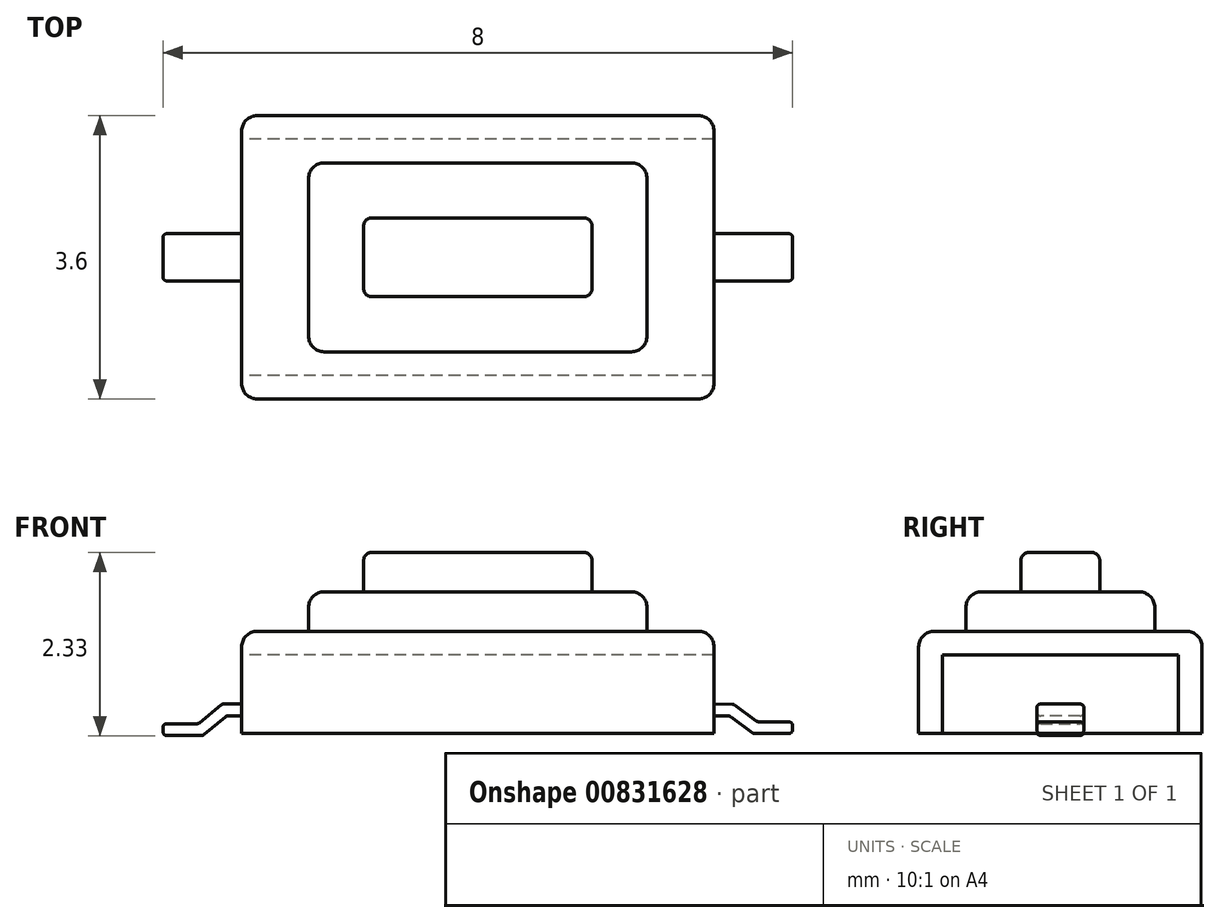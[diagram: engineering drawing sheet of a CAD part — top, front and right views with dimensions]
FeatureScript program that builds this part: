
annotation { "Feature Type Name" : "Feature", "Feature Type Description" : "" }
export const myFeature = defineFeature(function(context is Context, id is Id, definition is map)
    precondition{}
    {
        {
            var Q0;
            Q0=qCreatedBy(makeId("Top.planeOp"),FACE);
            var sketch = newSketch(context, id + "F0", { "sketchPlane" : qUnion([Q0])});
            skLineSegment(sketch, "E0.bottom", {"start": v(3, -1.5) * mm, "end": v(-3, -1.5) * mm});
            skLineSegment(sketch, "E0.top", {"start": v(3, 1.5) * mm, "end": v(-3, 1.5) * mm});
            skLineSegment(sketch, "E0.left", {"start": v(3, -1.5) * mm, "end": v(3, 1.5) * mm});
            skLineSegment(sketch, "E0.right", {"start": v(-3, -1.5) * mm, "end": v(-3, 1.5) * mm});
            skPoint(sketch, "E0.middle", {"position": v(0, 0) * mm});
            skSolve(sketch);
        }
        {
            var Q0;
            Q0 = qSketchRegion(id + "F0", true);
            extrude(context, id + "F1", {"entities" : qUnion([Q0]), "depth" : 1 * mm, "offsetDistance" : 25 * mm});
        }
        {
            var Q0;
            Q0=makeQuery(id+"F1.opExtrude","SWEPT_FACE",FACE,{"disambiguationData":[OSD([sQuery(id+"F0.wireOp",EDGE,"E0.right")])]});
            var sketch = newSketch(context, id + "F2", { "sketchPlane" : qUnion([Q0])});
            skLineSegment(sketch, "E1", {"start": v(-1.5, 0) * mm, "end": v(-1.8, 0) * mm});
            skLineSegment(sketch, "E2", {"start": v(-1.8, 0) * mm, "end": v(-1.8, 1.3) * mm});
            skLineSegment(sketch, "E3", {"start": v(-1.8, 1.3) * mm, "end": v(1.8, 1.3) * mm});
            skLineSegment(sketch, "E4", {"start": v(1.8, 1.3) * mm, "end": v(1.8, 0) * mm});
            skLineSegment(sketch, "E5", {"start": v(1.8, 0) * mm, "end": v(1.5, 0) * mm});
            skLineSegment(sketch, "E6", {"start": v(-1.5, 0) * mm, "end": v(-1.5, 1) * mm});
            skLineSegment(sketch, "E7", {"start": v(-1.5, 1) * mm, "end": v(1.5, 1) * mm});
            skLineSegment(sketch, "E8", {"start": v(1.5, 1) * mm, "end": v(1.5, 0) * mm});
            skSolve(sketch);
        }
        {
            var Q0;
            Q0=makeQuery(id+"F2.imprint","IMPRINT",FACE,{"disambiguationData":[TD([[makeQuery(id+"F2.imprint","IMPRINT",EDGE,{"derivedFrom":sQuery(id+"F2.wireOp",EDGE,"E1")}),-1.0]])]});
            extrude(context, id + "F3", {"entities" : qUnion([Q0]), "oppositeDirection" : true, "depth" : 6 * mm, "offsetDistance" : 25 * mm});
        }
        {
            var Q0;
            Q0=makeQuery(id+"F3.opExtrude","SWEPT_FACE",FACE,{"disambiguationData":[OSD([sQuery(id+"F2.wireOp",EDGE,"E3")])]});
            var sketch = newSketch(context, id + "F4", { "sketchPlane" : qUnion([Q0])});
            skLineSegment(sketch, "E9.bottom", {"start": v(1.95, -1.2) * mm, "end": v(-1.95, -1.2) * mm});
            skLineSegment(sketch, "E9.top", {"start": v(1.95, 1.2) * mm, "end": v(-1.95, 1.2) * mm});
            skLineSegment(sketch, "E9.left", {"start": v(2.15, -1) * mm, "end": v(2.15, 1) * mm});
            skLineSegment(sketch, "E9.right", {"start": v(-2.15, -1) * mm, "end": v(-2.15, 1) * mm});
            skPoint(sketch, "E9.middle", {"position": v(0, 0) * mm});
            skPoint(sketch, "E10.visualSharp", {"position": v(2.15, 1.2) * mm});
            skArc(sketch, "E10.filletArc", {"start": v(2.15, 1) * mm, "mid": v(2.1, 1.14) * mm, "end": v(1.95, 1.2) * mm});
            skPoint(sketch, "E11.visualSharp", {"position": v(2.15, -1.2) * mm});
            skArc(sketch, "E11.filletArc", {"start": v(1.95, -1.2) * mm, "mid": v(2.1, -1.14) * mm, "end": v(2.15, -1) * mm});
            skPoint(sketch, "E12.visualSharp", {"position": v(-2.15, 1.2) * mm});
            skArc(sketch, "E12.filletArc", {"start": v(-1.95, 1.2) * mm, "mid": v(-2.1, 1.14) * mm, "end": v(-2.15, 1) * mm});
            skPoint(sketch, "E13.visualSharp", {"position": v(-2.15, -1.2) * mm});
            skArc(sketch, "E13.filletArc", {"start": v(-2.15, -1) * mm, "mid": v(-2.1, -1.14) * mm, "end": v(-1.95, -1.2) * mm});
            skSolve(sketch);
        }
        {
            var Q0;
            Q0=makeQuery(id+"F4.imprint","IMPRINT",FACE,{"disambiguationData":[TD([[makeQuery(id+"F4.imprint","IMPRINT",EDGE,{"derivedFrom":sQuery(id+"F4.wireOp",EDGE,"E9.bottom")}),-1.0]])]});
            extrude(context, id + "F5", {"entities" : qUnion([Q0]), "operationType" : NewBodyOperationType.ADD, "depth" : 0.5 * mm, "offsetDistance" : 25 * mm});
        }
        {
            var Q0;
            Q0=makeQuery(id+"F5.opExtrude","CAP_FACE",FACE,{"disambiguationData":[OSD([sQuery(id+"F4.wireOp",EDGE,"E9.bottom"),sQuery(id+"F4.wireOp",EDGE,"E9.top"),sQuery(id+"F4.wireOp",EDGE,"E9.left"),sQuery(id+"F4.wireOp",EDGE,"E9.right"),sQuery(id+"F4.wireOp",EDGE,"E10.filletArc"),sQuery(id+"F4.wireOp",EDGE,"E11.filletArc"),sQuery(id+"F4.wireOp",EDGE,"E12.filletArc"),sQuery(id+"F4.wireOp",EDGE,"E13.filletArc")])],"isStart":false});
            fillet(context, id + "F6", {"entities" : qUnion([Q0]), "radius" : 0.2 * mm, "tangentPropagation" : true, "allowEdgeOverflow" : false});
        }
        {
            var Q0;
            Q0=makeQuery(id+"F5.opExtrude","CAP_FACE",FACE,{"disambiguationData":[OSD([sQuery(id+"F4.wireOp",EDGE,"E9.bottom"),sQuery(id+"F4.wireOp",EDGE,"E9.top"),sQuery(id+"F4.wireOp",EDGE,"E9.left"),sQuery(id+"F4.wireOp",EDGE,"E9.right"),sQuery(id+"F4.wireOp",EDGE,"E10.filletArc"),sQuery(id+"F4.wireOp",EDGE,"E11.filletArc"),sQuery(id+"F4.wireOp",EDGE,"E12.filletArc"),sQuery(id+"F4.wireOp",EDGE,"E13.filletArc")])],"isStart":false});
            var sketch = newSketch(context, id + "F7", { "sketchPlane" : qUnion([Q0])});
            skLineSegment(sketch, "E14.0", {"start": v(-1.45, 0.5) * mm, "end": v(-1.45, -0.5) * mm});
            skLineSegment(sketch, "E14.1", {"start": v(1.45, 0.5) * mm, "end": v(-1.45, 0.5) * mm});
            skLineSegment(sketch, "E14.2", {"start": v(1.45, -0.5) * mm, "end": v(1.45, 0.5) * mm});
            skLineSegment(sketch, "E14.3", {"start": v(-1.45, -0.5) * mm, "end": v(1.45, -0.5) * mm});
            skSolve(sketch);
        }
        {
            var Q0;
            Q0 = qSketchRegion(id + "F7", true);
            extrude(context, id + "F8", {"entities" : qUnion([Q0]), "depth" : 0.5 * mm, "offsetDistance" : 25 * mm});
        }
        {
            var Q0;
            Q0=makeQuery(id+"F3.opExtrude","SWEPT_EDGE",EDGE,{"disambiguationData":[OSD([sQuery(id+"F2.wireOp",EDGE,"E3"),sQuery(id+"F2.wireOp",EDGE,"E4")])]});
            var Q1;
            Q1=makeQuery(id+"F3.opExtrude","SWEPT_EDGE",EDGE,{"disambiguationData":[OSD([sQuery(id+"F2.wireOp",EDGE,"E2"),sQuery(id+"F2.wireOp",EDGE,"E3")])]});
            fillet(context, id + "F9", {"entities" : qUnion([Q0, Q1]), "radius" : 0.2 * mm, "tangentPropagation" : true, "allowEdgeOverflow" : false});
        }
        {
            var Q0;
            Q0=makeQuery(id+"F1.opExtrude","SWEPT_FACE",FACE,{"disambiguationData":[OSD([sQuery(id+"F0.wireOp",EDGE,"E0.left")])]});
            var sketch = newSketch(context, id + "F10", { "sketchPlane" : qUnion([Q0])});
            skLineSegment(sketch, "E15", {"start": v(0, 0) * mm, "end": v(0, 0.3) * mm, "construction": true});
            skLineSegment(sketch, "E16.bottom", {"start": v(0.3, 0.38) * mm, "end": v(-0.3, 0.37) * mm});
            skLineSegment(sketch, "E16.top", {"start": v(0.3, 0.23) * mm, "end": v(-0.3, 0.22) * mm});
            skLineSegment(sketch, "E16.left", {"start": v(0.3, 0.38) * mm, "end": v(0.3, 0.23) * mm});
            skLineSegment(sketch, "E16.right", {"start": v(-0.3, 0.37) * mm, "end": v(-0.3, 0.22) * mm});
            skPoint(sketch, "E16.middle", {"position": v(0, 0.3) * mm});
            skSolve(sketch);
        }
        {
            var Q0;
            Q0=makeQuery(id+"F3.opExtrude","SWEPT_FACE",FACE,{"disambiguationData":[OSD([sQuery(id+"F2.wireOp",EDGE,"E4")])]});
            var sketch = newSketch(context, id + "F11", { "sketchPlane" : qUnion([Q0])});
            skLineSegment(sketch, "E17", {"start": v(3, 0.23) * mm, "end": v(3.2, 0.22) * mm});
            skLineSegment(sketch, "E18", {"start": v(3.2, 0.22) * mm, "end": v(3.5, 0) * mm});
            skLineSegment(sketch, "E19", {"start": v(3.5, 0) * mm, "end": v(4, 0) * mm});
            skLineSegment(sketch, "E20", {"start": v(-3, 0.25) * mm, "end": v(-3.2, 0.25) * mm});
            skLineSegment(sketch, "E21", {"start": v(-3.2, 0.25) * mm, "end": v(-3.5, 0) * mm});
            skLineSegment(sketch, "E22", {"start": v(-3.5, 0) * mm, "end": v(-4, 0) * mm});
            skSolve(sketch);
        }
        {
            var Q0;
            Q0=makeQuery(id+"F10.imprint","IMPRINT",FACE,{"disambiguationData":[TD([[makeQuery(id+"F10.imprint","IMPRINT",EDGE,{"derivedFrom":sQuery(id+"F10.wireOp",EDGE,"E16.bottom")}),1.0]])]});
            var Q1;
            Q1=sQuery(id+"F11.wireOp",EDGE,"E19");
            var Q2;
            Q2=sQuery(id+"F11.wireOp",EDGE,"E18");
            var Q3;
            Q3=sQuery(id+"F11.wireOp",EDGE,"E17");
            sweep(context, id + "F12", {"profiles" : qUnion([Q0]), "path" : qUnion([Q1, Q2, Q3])});
        }
        {
            var Q0;
            Q0=makeQuery(id+"F1.opExtrude","SWEPT_FACE",FACE,{"disambiguationData":[OSD([sQuery(id+"F0.wireOp",EDGE,"E0.right")])]});
            var sketch = newSketch(context, id + "F13", { "sketchPlane" : qUnion([Q0])});
            skLineSegment(sketch, "E23", {"start": v(0, 0) * mm, "end": v(0, 0.3) * mm, "construction": true});
            skLineSegment(sketch, "E24.bottom", {"start": v(0.3, 0.38) * mm, "end": v(-0.3, 0.37) * mm});
            skLineSegment(sketch, "E24.top", {"start": v(0.3, 0.23) * mm, "end": v(-0.3, 0.22) * mm});
            skLineSegment(sketch, "E24.left", {"start": v(0.3, 0.38) * mm, "end": v(0.3, 0.23) * mm});
            skLineSegment(sketch, "E24.right", {"start": v(-0.3, 0.37) * mm, "end": v(-0.3, 0.22) * mm});
            skPoint(sketch, "E24.middle", {"position": v(0, 0.3) * mm});
            skSolve(sketch);
        }
        {
            var Q0;
            Q0=makeQuery(id+"F13.imprint","IMPRINT",FACE,{"disambiguationData":[TD([[makeQuery(id+"F13.imprint","IMPRINT",EDGE,{"derivedFrom":sQuery(id+"F13.wireOp",EDGE,"E24.bottom")}),1.0]])]});
            var Q1;
            Q1=sQuery(id+"F11.wireOp",EDGE,"E20");
            var Q2;
            Q2=sQuery(id+"F11.wireOp",EDGE,"E21");
            var Q3;
            Q3=sQuery(id+"F11.wireOp",EDGE,"E22");
            sweep(context, id + "F14", {"profiles" : qUnion([Q0]), "path" : qUnion([Q1, Q2, Q3])});
        }
        {
            var Q0;
            Q0=makeQuery(id+"F3.opExtrude","CAP_EDGE",EDGE,{"disambiguationData":[OSD([sQuery(id+"F2.wireOp",EDGE,"E2")])],"isStart":true});
            var Q1;
            {var subQ0=sQuery(id+"F2.wireOp",EDGE,"E3");var subQ1=sQuery(id+"F2.wireOp",EDGE,"E2");Q1=makeQuery(id+"F9.opFillet","BLEND_EDGE",EDGE,{"blendedFrom":[makeQuery(id+"F3.opExtrude","SWEPT_EDGE",EDGE,{"disambiguationData":[OSD([subQ1,subQ0])]}),makeQuery(id+"F3.opExtrude","CAP_FACE",FACE,{"disambiguationData":[OSD([sQuery(id+"F2.wireOp",EDGE,"E1"),subQ1,subQ0,sQuery(id+"F2.wireOp",EDGE,"E4"),sQuery(id+"F2.wireOp",EDGE,"E5"),sQuery(id+"F2.wireOp",EDGE,"E6"),sQuery(id+"F2.wireOp",EDGE,"E7"),sQuery(id+"F2.wireOp",EDGE,"E8")])],"isStart":true})],"blendedInto":[makeQuery(id+"F3.opExtrude","CAP_FACE",FACE,{"disambiguationData":[OSD([sQuery(id+"F2.wireOp",EDGE,"E1"),subQ1,subQ0,sQuery(id+"F2.wireOp",EDGE,"E4"),sQuery(id+"F2.wireOp",EDGE,"E5"),sQuery(id+"F2.wireOp",EDGE,"E6"),sQuery(id+"F2.wireOp",EDGE,"E7"),sQuery(id+"F2.wireOp",EDGE,"E8")])],"isStart":true})]});}
            var Q2;
            Q2=makeQuery(id+"F3.opExtrude","CAP_EDGE",EDGE,{"disambiguationData":[OSD([sQuery(id+"F2.wireOp",EDGE,"E3")])],"isStart":true});
            var Q3;
            Q3=makeQuery(id+"F3.opExtrude","CAP_EDGE",EDGE,{"disambiguationData":[OSD([sQuery(id+"F2.wireOp",EDGE,"E4")])],"isStart":true});
            var Q4;
            {var subQ0=sQuery(id+"F2.wireOp",EDGE,"E4");var subQ1=sQuery(id+"F2.wireOp",EDGE,"E3");Q4=makeQuery(id+"F9.opFillet","BLEND_EDGE",EDGE,{"blendedFrom":[makeQuery(id+"F3.opExtrude","SWEPT_EDGE",EDGE,{"disambiguationData":[OSD([subQ1,subQ0])]}),makeQuery(id+"F3.opExtrude","CAP_FACE",FACE,{"disambiguationData":[OSD([sQuery(id+"F2.wireOp",EDGE,"E1"),sQuery(id+"F2.wireOp",EDGE,"E2"),subQ1,subQ0,sQuery(id+"F2.wireOp",EDGE,"E5"),sQuery(id+"F2.wireOp",EDGE,"E6"),sQuery(id+"F2.wireOp",EDGE,"E7"),sQuery(id+"F2.wireOp",EDGE,"E8")])],"isStart":true})],"blendedInto":[makeQuery(id+"F3.opExtrude","CAP_FACE",FACE,{"disambiguationData":[OSD([sQuery(id+"F2.wireOp",EDGE,"E1"),sQuery(id+"F2.wireOp",EDGE,"E2"),subQ1,subQ0,sQuery(id+"F2.wireOp",EDGE,"E5"),sQuery(id+"F2.wireOp",EDGE,"E6"),sQuery(id+"F2.wireOp",EDGE,"E7"),sQuery(id+"F2.wireOp",EDGE,"E8")])],"isStart":true})]});}
            var Q5;
            Q5=makeQuery(id+"F3.opExtrude","CAP_EDGE",EDGE,{"disambiguationData":[OSD([sQuery(id+"F2.wireOp",EDGE,"E3")])],"isStart":false});
            fillet(context, id + "F15", {"entities" : qUnion([Q0, Q1, Q2, Q3, Q4, Q5]), "radius" : 0.2 * mm, "tangentPropagation" : true, "allowEdgeOverflow" : false});
        }
        {
            var Q0;
            Q0=makeQuery(id+"F8.opExtrude","CAP_EDGE",EDGE,{"disambiguationData":[OSD([sQuery(id+"F7.wireOp",EDGE,"E14.3")])],"isStart":false});
            var Q1;
            Q1=makeQuery(id+"F8.opExtrude","CAP_EDGE",EDGE,{"disambiguationData":[OSD([sQuery(id+"F7.wireOp",EDGE,"E14.1")])],"isStart":false});
            var Q2;
            Q2=makeQuery(id+"F8.opExtrude","CAP_EDGE",EDGE,{"disambiguationData":[OSD([sQuery(id+"F7.wireOp",EDGE,"E14.0")])],"isStart":false});
            var Q3;
            Q3=makeQuery(id+"F8.opExtrude","CAP_EDGE",EDGE,{"disambiguationData":[OSD([sQuery(id+"F7.wireOp",EDGE,"E14.2")])],"isStart":false});
            var Q4;
            Q4=makeQuery(id+"F8.opExtrude","SWEPT_EDGE",EDGE,{"disambiguationData":[OSD([sQuery(id+"F7.wireOp",EDGE,"E14.0"),sQuery(id+"F7.wireOp",EDGE,"E14.1")])]});
            var Q5;
            Q5=makeQuery(id+"F8.opExtrude","SWEPT_EDGE",EDGE,{"disambiguationData":[OSD([sQuery(id+"F7.wireOp",EDGE,"E14.1"),sQuery(id+"F7.wireOp",EDGE,"E14.2")])]});
            var Q6;
            Q6=makeQuery(id+"F8.opExtrude","SWEPT_EDGE",EDGE,{"disambiguationData":[OSD([sQuery(id+"F7.wireOp",EDGE,"E14.0"),sQuery(id+"F7.wireOp",EDGE,"E14.3")])]});
            var Q7;
            Q7=makeQuery(id+"F8.opExtrude","SWEPT_EDGE",EDGE,{"disambiguationData":[OSD([sQuery(id+"F7.wireOp",EDGE,"E14.2"),sQuery(id+"F7.wireOp",EDGE,"E14.3")])]});
            fillet(context, id + "F16", {"entities" : qUnion([Q0, Q1, Q2, Q3, Q4, Q5, Q6, Q7]), "radius" : 0.1 * mm, "tangentPropagation" : true, "allowEdgeOverflow" : false});
        }
        {
            var Q0;
            Q0=makeQuery(id+"F14.opSweep","SWEPT_EDGE",EDGE,{"disambiguationData":[OSD([sQuery(id+"F11.wireOp",EDGE,"E21"),sQuery(id+"F13.wireOp",EDGE,"E24.bottom"),sQuery(id+"F13.wireOp",EDGE,"E24.right")])]});
            var Q1;
            Q1=makeQuery(id+"F14.opSweep","SWEPT_EDGE",EDGE,{"disambiguationData":[OSD([sQuery(id+"F11.wireOp",EDGE,"E22"),sQuery(id+"F13.wireOp",EDGE,"E24.bottom"),sQuery(id+"F13.wireOp",EDGE,"E24.right")])]});
            var Q2;
            Q2=makeQuery(id+"F14.opSweep","SWEPT_EDGE",EDGE,{"disambiguationData":[OSD([sQuery(id+"F11.wireOp",EDGE,"E20"),sQuery(id+"F13.wireOp",EDGE,"E24.bottom"),sQuery(id+"F13.wireOp",EDGE,"E24.right")])]});
            var Q3;
            Q3=makeQuery(id+"F14.opSweep","SWEPT_EDGE",EDGE,{"disambiguationData":[OSD([sQuery(id+"F11.wireOp",EDGE,"E22"),sQuery(id+"F13.wireOp",EDGE,"E24.bottom"),sQuery(id+"F13.wireOp",EDGE,"E24.left")])]});
            var Q4;
            Q4=makeQuery(id+"F14.opSweep","SWEPT_EDGE",EDGE,{"disambiguationData":[OSD([sQuery(id+"F11.wireOp",EDGE,"E21"),sQuery(id+"F13.wireOp",EDGE,"E24.bottom"),sQuery(id+"F13.wireOp",EDGE,"E24.left")])]});
            var Q5;
            Q5=makeQuery(id+"F14.opSweep","SWEPT_EDGE",EDGE,{"disambiguationData":[OSD([sQuery(id+"F11.wireOp",EDGE,"E20"),sQuery(id+"F13.wireOp",EDGE,"E24.bottom"),sQuery(id+"F13.wireOp",EDGE,"E24.left")])]});
            var Q6;
            Q6=makeQuery(id+"F14.opSweep","MID_CAP_EDGE",EDGE,{"disambiguationData":[OSD([sQuery(id+"F11.wireOp",VERTEX,"E21.start"),sQuery(id+"F13.wireOp",EDGE,"E24.bottom")])],"capPos":1.0});
            var Q7;
            Q7=makeQuery(id+"F14.opSweep","MID_CAP_EDGE",EDGE,{"disambiguationData":[OSD([sQuery(id+"F11.wireOp",VERTEX,"E22.start"),sQuery(id+"F13.wireOp",EDGE,"E24.bottom")])],"capPos":2.0});
            var Q8;
            Q8=makeQuery(id+"F14.opSweep","CAP_EDGE",EDGE,{"disambiguationData":[OSD([sQuery(id+"F11.wireOp",VERTEX,"E22.end"),sQuery(id+"F13.wireOp",EDGE,"E24.bottom")])],"isStart":false});
            var Q9;
            Q9=makeQuery(id+"F14.opSweep","MID_CAP_EDGE",EDGE,{"disambiguationData":[OSD([sQuery(id+"F11.wireOp",VERTEX,"E21.start"),sQuery(id+"F13.wireOp",EDGE,"E24.top")])],"capPos":1.0});
            var Q10;
            Q10=makeQuery(id+"F14.opSweep","MID_CAP_EDGE",EDGE,{"disambiguationData":[OSD([sQuery(id+"F11.wireOp",VERTEX,"E22.start"),sQuery(id+"F13.wireOp",EDGE,"E24.top")])],"capPos":2.0});
            var Q11;
            Q11=makeQuery(id+"F14.opSweep","SWEPT_EDGE",EDGE,{"disambiguationData":[OSD([sQuery(id+"F11.wireOp",EDGE,"E20"),sQuery(id+"F13.wireOp",EDGE,"E24.top"),sQuery(id+"F13.wireOp",EDGE,"E24.left")])]});
            var Q12;
            Q12=makeQuery(id+"F14.opSweep","SWEPT_EDGE",EDGE,{"disambiguationData":[OSD([sQuery(id+"F11.wireOp",EDGE,"E21"),sQuery(id+"F13.wireOp",EDGE,"E24.top"),sQuery(id+"F13.wireOp",EDGE,"E24.left")])]});
            var Q13;
            Q13=makeQuery(id+"F14.opSweep","SWEPT_EDGE",EDGE,{"disambiguationData":[OSD([sQuery(id+"F11.wireOp",EDGE,"E21"),sQuery(id+"F13.wireOp",EDGE,"E24.top"),sQuery(id+"F13.wireOp",EDGE,"E24.right")])]});
            var Q14;
            Q14=makeQuery(id+"F14.opSweep","CAP_EDGE",EDGE,{"disambiguationData":[OSD([sQuery(id+"F11.wireOp",VERTEX,"E22.end"),sQuery(id+"F13.wireOp",EDGE,"E24.top")])],"isStart":false});
            var Q15;
            Q15=makeQuery(id+"F14.opSweep","SWEPT_EDGE",EDGE,{"disambiguationData":[OSD([sQuery(id+"F11.wireOp",EDGE,"E22"),sQuery(id+"F13.wireOp",EDGE,"E24.top"),sQuery(id+"F13.wireOp",EDGE,"E24.right")])]});
            var Q16;
            Q16=makeQuery(id+"F14.opSweep","SWEPT_EDGE",EDGE,{"disambiguationData":[OSD([sQuery(id+"F11.wireOp",EDGE,"E22"),sQuery(id+"F13.wireOp",EDGE,"E24.top"),sQuery(id+"F13.wireOp",EDGE,"E24.left")])]});
            var Q17;
            Q17=makeQuery(id+"F14.opSweep","CAP_EDGE",EDGE,{"disambiguationData":[OSD([sQuery(id+"F11.wireOp",VERTEX,"E22.end"),sQuery(id+"F13.wireOp",EDGE,"E24.left")])],"isStart":false});
            var Q18;
            Q18=makeQuery(id+"F14.opSweep","CAP_EDGE",EDGE,{"disambiguationData":[OSD([sQuery(id+"F11.wireOp",VERTEX,"E22.end"),sQuery(id+"F13.wireOp",EDGE,"E24.right")])],"isStart":false});
            var Q19;
            Q19=makeQuery(id+"F14.opSweep","SWEPT_EDGE",EDGE,{"disambiguationData":[OSD([sQuery(id+"F11.wireOp",EDGE,"E20"),sQuery(id+"F13.wireOp",EDGE,"E24.top"),sQuery(id+"F13.wireOp",EDGE,"E24.right")])]});
            fillet(context, id + "F17", {"entities" : qUnion([Q0, Q1, Q2, Q3, Q4, Q5, Q6, Q7, Q8, Q9, Q10, Q11, Q12, Q13, Q14, Q15, Q16, Q17, Q18, Q19]), "radius" : 0.05 * mm, "tangentPropagation" : true, "allowEdgeOverflow" : false});
        }
        {
            var Q0;
            Q0=makeQuery(id+"F12.opSweep","SWEPT_EDGE",EDGE,{"disambiguationData":[OSD([sQuery(id+"F10.wireOp",EDGE,"E16.bottom"),sQuery(id+"F10.wireOp",EDGE,"E16.right"),sQuery(id+"F11.wireOp",EDGE,"E17")])]});
            var Q1;
            Q1=makeQuery(id+"F12.opSweep","SWEPT_EDGE",EDGE,{"disambiguationData":[OSD([sQuery(id+"F10.wireOp",EDGE,"E16.bottom"),sQuery(id+"F10.wireOp",EDGE,"E16.right"),sQuery(id+"F11.wireOp",EDGE,"E18")])]});
            var Q2;
            Q2=makeQuery(id+"F12.opSweep","SWEPT_EDGE",EDGE,{"disambiguationData":[OSD([sQuery(id+"F10.wireOp",EDGE,"E16.bottom"),sQuery(id+"F10.wireOp",EDGE,"E16.right"),sQuery(id+"F11.wireOp",EDGE,"E19")])]});
            var Q3;
            Q3=makeQuery(id+"F12.opSweep","CAP_EDGE",EDGE,{"disambiguationData":[OSD([sQuery(id+"F10.wireOp",EDGE,"E16.bottom"),sQuery(id+"F11.wireOp",VERTEX,"E19.end")])],"isStart":false});
            var Q4;
            Q4=makeQuery(id+"F12.opSweep","MID_CAP_EDGE",EDGE,{"disambiguationData":[OSD([sQuery(id+"F10.wireOp",EDGE,"E16.bottom"),sQuery(id+"F11.wireOp",VERTEX,"E17.end")])],"capPos":1.0});
            var Q5;
            Q5=makeQuery(id+"F12.opSweep","MID_CAP_EDGE",EDGE,{"disambiguationData":[OSD([sQuery(id+"F10.wireOp",EDGE,"E16.bottom"),sQuery(id+"F11.wireOp",VERTEX,"E18.end")])],"capPos":2.0});
            var Q6;
            Q6=makeQuery(id+"F12.opSweep","SWEPT_EDGE",EDGE,{"disambiguationData":[OSD([sQuery(id+"F10.wireOp",EDGE,"E16.bottom"),sQuery(id+"F10.wireOp",EDGE,"E16.left"),sQuery(id+"F11.wireOp",EDGE,"E17")])]});
            var Q7;
            Q7=makeQuery(id+"F12.opSweep","SWEPT_EDGE",EDGE,{"disambiguationData":[OSD([sQuery(id+"F10.wireOp",EDGE,"E16.bottom"),sQuery(id+"F10.wireOp",EDGE,"E16.left"),sQuery(id+"F11.wireOp",EDGE,"E18")])]});
            var Q8;
            Q8=makeQuery(id+"F12.opSweep","SWEPT_EDGE",EDGE,{"disambiguationData":[OSD([sQuery(id+"F10.wireOp",EDGE,"E16.bottom"),sQuery(id+"F10.wireOp",EDGE,"E16.left"),sQuery(id+"F11.wireOp",EDGE,"E19")])]});
            var Q9;
            Q9=makeQuery(id+"F12.opSweep","CAP_EDGE",EDGE,{"disambiguationData":[OSD([sQuery(id+"F10.wireOp",EDGE,"E16.left"),sQuery(id+"F11.wireOp",VERTEX,"E19.end")])],"isStart":false});
            var Q10;
            Q10=makeQuery(id+"F12.opSweep","SWEPT_EDGE",EDGE,{"disambiguationData":[OSD([sQuery(id+"F10.wireOp",EDGE,"E16.top"),sQuery(id+"F10.wireOp",EDGE,"E16.left"),sQuery(id+"F11.wireOp",EDGE,"E19")])]});
            var Q11;
            Q11=makeQuery(id+"F12.opSweep","SWEPT_EDGE",EDGE,{"disambiguationData":[OSD([sQuery(id+"F10.wireOp",EDGE,"E16.top"),sQuery(id+"F10.wireOp",EDGE,"E16.left"),sQuery(id+"F11.wireOp",EDGE,"E18")])]});
            var Q12;
            Q12=makeQuery(id+"F12.opSweep","SWEPT_EDGE",EDGE,{"disambiguationData":[OSD([sQuery(id+"F10.wireOp",EDGE,"E16.top"),sQuery(id+"F10.wireOp",EDGE,"E16.left"),sQuery(id+"F11.wireOp",EDGE,"E17")])]});
            var Q13;
            Q13=makeQuery(id+"F12.opSweep","CAP_EDGE",EDGE,{"disambiguationData":[OSD([sQuery(id+"F10.wireOp",EDGE,"E16.right"),sQuery(id+"F11.wireOp",VERTEX,"E19.end")])],"isStart":false});
            var Q14;
            Q14=makeQuery(id+"F12.opSweep","SWEPT_EDGE",EDGE,{"disambiguationData":[OSD([sQuery(id+"F10.wireOp",EDGE,"E16.top"),sQuery(id+"F10.wireOp",EDGE,"E16.right"),sQuery(id+"F11.wireOp",EDGE,"E17")])]});
            var Q15;
            Q15=makeQuery(id+"F12.opSweep","SWEPT_EDGE",EDGE,{"disambiguationData":[OSD([sQuery(id+"F10.wireOp",EDGE,"E16.top"),sQuery(id+"F10.wireOp",EDGE,"E16.right"),sQuery(id+"F11.wireOp",EDGE,"E18")])]});
            var Q16;
            Q16=makeQuery(id+"F12.opSweep","SWEPT_EDGE",EDGE,{"disambiguationData":[OSD([sQuery(id+"F10.wireOp",EDGE,"E16.top"),sQuery(id+"F10.wireOp",EDGE,"E16.right"),sQuery(id+"F11.wireOp",EDGE,"E19")])]});
            var Q17;
            Q17=makeQuery(id+"F12.opSweep","CAP_EDGE",EDGE,{"disambiguationData":[OSD([sQuery(id+"F10.wireOp",EDGE,"E16.top"),sQuery(id+"F11.wireOp",VERTEX,"E19.end")])],"isStart":false});
            var Q18;
            Q18=makeQuery(id+"F12.opSweep","MID_CAP_EDGE",EDGE,{"disambiguationData":[OSD([sQuery(id+"F10.wireOp",EDGE,"E16.top"),sQuery(id+"F11.wireOp",VERTEX,"E17.end")])],"capPos":1.0});
            var Q19;
            Q19=makeQuery(id+"F12.opSweep","SWEPT_FACE",FACE,{"disambiguationData":[OSD([sQuery(id+"F10.wireOp",EDGE,"E16.top"),sQuery(id+"F11.wireOp",EDGE,"E18")])]});
            fillet(context, id + "F18", {"entities" : qUnion([Q0, Q1, Q2, Q3, Q4, Q5, Q6, Q7, Q8, Q9, Q10, Q11, Q12, Q13, Q14, Q15, Q16, Q17, Q18, Q19]), "radius" : 0.05 * mm, "tangentPropagation" : true, "allowEdgeOverflow" : false});
        }
    });
